# Revit family: VUTRVUER 351 PE EC – копія
name_source: partatom
category: Mechanical Equipment
units: mm (PartAtom-declared; Revit-internal decimal feet)

## family parameters
Always vertical = Yes
Cut with Voids When Loaded = No
OmniClass Number = 23.75.00.00
OmniClass Title = Climate Control (HVAC)
Part Type = Normal
Room Calculation Point = No
Round Connector Dimension = Use Diameter
Shared = No
Work Plane-Based = No

## types (4) — shared parameters
00_20_Manufacturer = Blauberg
00_20_Name = Single-room air handling unit with heat recovery
A = 1170 mm  [stored 3.83858 ft]
A1 = 1270 mm
A2 = 1110 mm  [stored 3.64173 ft]
B = 700 mm  [stored 2.29659 ft]
B1 = 756 mm  [stored 2.48031 ft]
B2 = 752 mm  [stored 2.46719 ft]
C = 145 mm  [stored 0.475722 ft]
C1 = 190 mm
C2 = 285 mm  [stored 0.935039 ft]
C3 = 225 mm  [stored 0.738189 ft]
Casing Material = Polymer-coated steel (white)
D = 200 mm  [stored 0.656168 ft]
D1 = 123 mm  [stored 0.403543 ft]
D2 = 9 mm  [stored 0.0295276 ft]
E = 203 mm  [stored 0.66601 ft]
E1 = 390 mm  [stored 1.27953 ft]
Filter = G4
Frequency = 60 Hz
H = 310 mm  [stored 1.01706 ft]
Load Classification = HVAC
Maintenance zone material = <By Category>
Maximum Air Flow = 513.0 m³/h
Number of Fase = 1
Sound pressure level at 3 m distance = 31 dBA
Voltage = 230 V
Weight = 72.00 kg
zero-valued in all types: Default Elevation

## per-type parameters (varying)
| type | Amperage | Power |
| Komfort Roto EC D 351 S21 | 2 A | 247 W |
| Komfort Roto EC D 351-E S21 | 2 A | 247 W |
| Komfort Roto EC DE 351 S21 | 7 A | 1447 W |
| Komfort Roto EC DE 351-E S21 | 7 A | 1447 W |

note: column(s) folded — value = type name in every type: 00_20_Type

note: [stored X ft] marks values corroborated as IEEE doubles in the binary element streams (Revit-internal decimal feet)

## geometry (parser evidence)
native form markers: Sweep x15
no freeform markers — native parametric forms only
